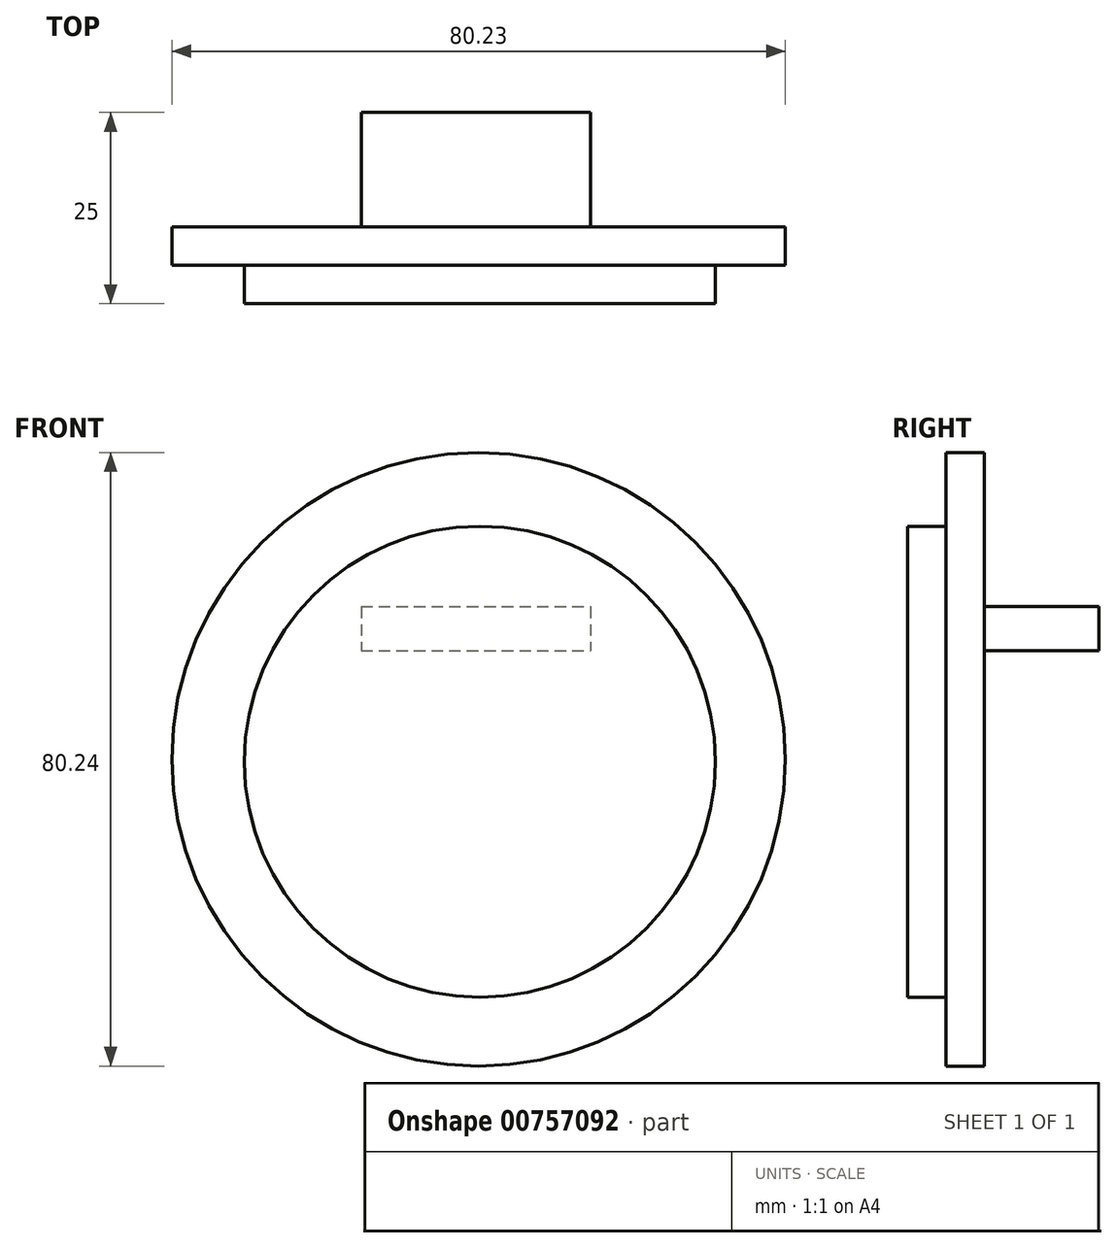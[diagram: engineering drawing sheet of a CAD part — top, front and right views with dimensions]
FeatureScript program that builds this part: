
annotation { "Feature Type Name" : "Feature", "Feature Type Description" : "" }
export const myFeature = defineFeature(function(context is Context, id is Id, definition is map)
    precondition{}
    {
        {
            var Q0;
            Q0=qCreatedBy(makeId("Front.planeOp"),FACE);
            var sketch = newSketch(context, id + "F0", { "sketchPlane" : qUnion([Q0])});
            skCircle(sketch, "E0", {"center": v(-24.1, 22.16) * mm, "radius": 30.8 * mm});
            skSolve(sketch);
        }
        {
            var Q0;
            Q0 = qSketchRegion(id + "F0", true);
            extrude(context, id + "F1", {"entities" : qUnion([Q0]), "depth" : 5 * mm, "offsetDistance" : 25.4 * mm});
        }
        {
            var Q0;
            Q0=qCreatedBy(makeId("Front.planeOp"),FACE);
            var sketch = newSketch(context, id + "F2", { "sketchPlane" : qUnion([Q0])});
            skCircle(sketch, "E1", {"center": v(-24.27, 22.47) * mm, "radius": 40.12 * mm});
            skPoint(sketch, "E1.first.point", {"position": v(-29.07, 62.3) * mm});
            skPoint(sketch, "E1.second.point", {"position": v(-19.78, -17.4) * mm});
            skPoint(sketch, "E1.third.point", {"position": v(-31.4, -17) * mm});
            skPoint(sketch, "E2", {"position": v(-25.58, -17.62) * mm});
            skSolve(sketch);
        }
        {
            var Q0;
            Q0 = qSketchRegion(id + "F2", true);
            extrude(context, id + "F3", {"entities" : qUnion([Q0]), "operationType" : NewBodyOperationType.ADD, "oppositeDirection" : true, "depth" : 5 * mm, "offsetDistance" : 25.4 * mm});
        }
        {
            var Q0;
            Q0=qCreatedBy(makeId("Front.planeOp"),FACE);
            var sketch = newSketch(context, id + "F4", { "sketchPlane" : qUnion([Q0])});
            skLineSegment(sketch, "E3.bottom", {"start": v(-39.61, 42.43) * mm, "end": v(-9.61, 42.43) * mm});
            skLineSegment(sketch, "E3.top", {"start": v(-39.61, 36.69) * mm, "end": v(-9.61, 36.69) * mm});
            skLineSegment(sketch, "E3.left", {"start": v(-39.61, 42.43) * mm, "end": v(-39.61, 36.69) * mm});
            skLineSegment(sketch, "E3.right", {"start": v(-9.61, 42.43) * mm, "end": v(-9.61, 36.69) * mm});
            skPoint(sketch, "E4", {"position": v(-22.64, 42.43) * mm});
            skPoint(sketch, "E5", {"position": v(-20.9, 36.69) * mm});
            skPoint(sketch, "E6", {"position": v(-39.61, 39.56) * mm});
            skPoint(sketch, "E7", {"position": v(-9.61, 39.56) * mm});
            skSolve(sketch);
        }
        {
            var Q0;
            Q0 = qSketchRegion(id + "F4", true);
            extrude(context, id + "F5", {"entities" : qUnion([Q0]), "operationType" : NewBodyOperationType.ADD, "oppositeDirection" : true, "depth" : 20 * mm, "offsetDistance" : 25.4 * mm});
        }
    });
